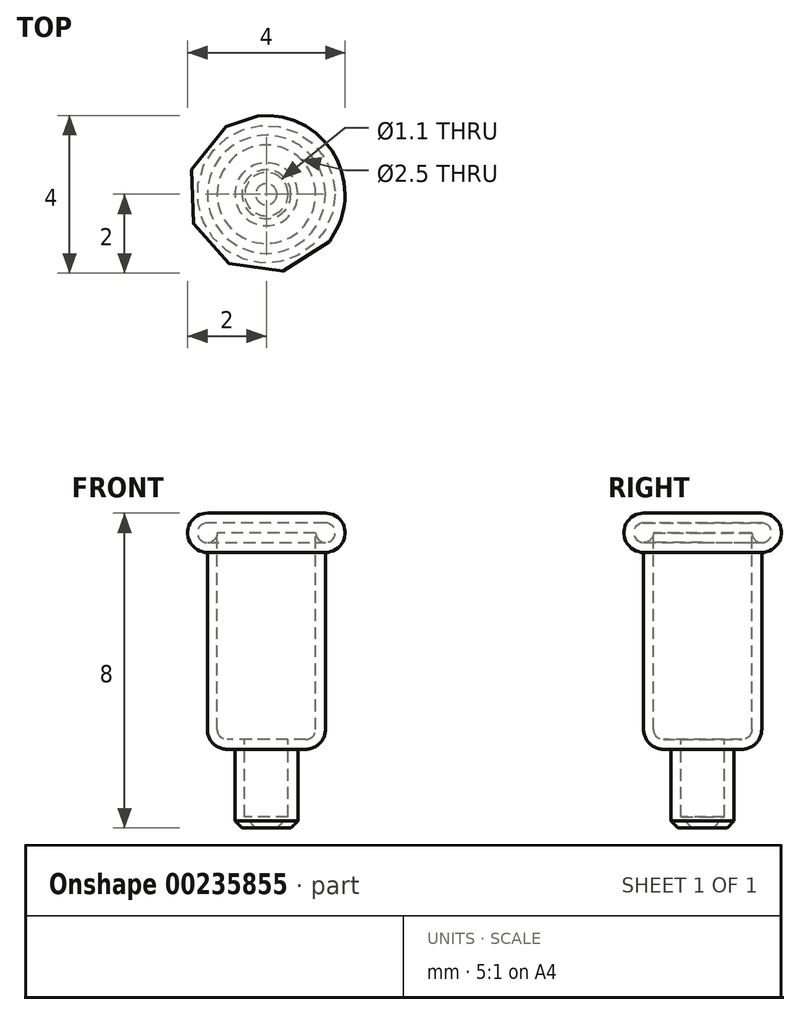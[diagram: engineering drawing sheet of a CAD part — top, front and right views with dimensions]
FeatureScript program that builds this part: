
annotation { "Feature Type Name" : "Feature", "Feature Type Description" : "" }
export const myFeature = defineFeature(function(context is Context, id is Id, definition is map)
    precondition{}
    {
        {
            var Q0;
            Q0=qCreatedBy(makeId("Front.planeOp"),FACE);
            var sketch = newSketch(context, id + "F0", { "sketchPlane" : qUnion([Q0])});
            skLineSegment(sketch, "E0", {"start": v(0, 0) * mm, "end": v(0, -8) * mm});
            skLineSegment(sketch, "E1", {"start": v(0, 0) * mm, "end": v(-1.5, 0) * mm});
            skLineSegment(sketch, "E2", {"start": v(-2, -0.5) * mm, "end": v(-2, -0.5) * mm});
            skLineSegment(sketch, "E3.0", {"start": v(-1.5, -1) * mm, "end": v(-1.5, -5.5) * mm});
            skLineSegment(sketch, "E4.0", {"start": v(-0.8, -6) * mm, "end": v(-0.8, -7.82) * mm});
            skLineSegment(sketch, "E5.0", {"start": v(-0.8, -6) * mm, "end": v(-1, -6) * mm});
            skLineSegment(sketch, "E6.trimOffspring", {"start": v(-1.5, -1) * mm, "end": v(-1.5, -1) * mm});
            skLineSegment(sketch, "E7.0", {"start": v(-1.25, -0.5) * mm, "end": v(-1.25, -5.5) * mm});
            skLineSegment(sketch, "E8.0", {"start": v(0, -0.25) * mm, "end": v(-1.5, -0.25) * mm});
            skLineSegment(sketch, "E9", {"start": v(-0.55, -5.75) * mm, "end": v(-1, -5.75) * mm});
            skLineSegment(sketch, "E10", {"start": v(-1.25, -0.5) * mm, "end": v(0, -0.5) * mm, "construction": true});
            skArc(sketch, "E11.filletArc", {"start": v(-1.5, 0) * mm, "mid": v(-1.85, -0.15) * mm, "end": v(-2, -0.5) * mm});
            skPoint(sketch, "E12.visualSharp", {"position": v(-2, -1) * mm});
            skArc(sketch, "E12.filletArc", {"start": v(-2, -0.5) * mm, "mid": v(-1.85, -0.85) * mm, "end": v(-1.5, -1) * mm});
            skArc(sketch, "E13", {"start": v(-1.5, -0.25) * mm, "mid": v(-1.68, -0.68) * mm, "end": v(-1.25, -0.5) * mm});
            skArc(sketch, "E14.filletArc", {"start": v(-1.5, -5.5) * mm, "mid": v(-1.35, -5.85) * mm, "end": v(-1, -6) * mm});
            skArc(sketch, "E15", {"start": v(-1.25, -5.5) * mm, "mid": v(-1.18, -5.68) * mm, "end": v(-1, -5.75) * mm});
            skLineSegment(sketch, "E16", {"start": v(-0.55, -5.75) * mm, "end": v(0, -5.75) * mm, "construction": true});
            skLineSegment(sketch, "E17.0", {"start": v(-0.55, -5.75) * mm, "end": v(-0.55, -7.72) * mm});
            skLineSegment(sketch, "E18", {"start": v(-0.27, -8) * mm, "end": v(-0.62, -8) * mm, "construction": true});
            skLineSegment(sketch, "E19", {"start": v(-0.62, -8) * mm, "end": v(-0.8, -7.82) * mm});
            skLineSegment(sketch, "E20", {"start": v(-0.27, -8) * mm, "end": v(-0.55, -7.72) * mm});
            skLineSegment(sketch, "E21", {"start": v(-0.27, -8) * mm, "end": v(-0.6, -8) * mm});
            skLineSegment(sketch, "E22", {"start": v(-0.6, -8) * mm, "end": v(-0.6, -6) * mm, "construction": true});
            skLineSegment(sketch, "E23", {"start": v(-0.8, -6) * mm, "end": v(0, -6) * mm, "construction": true});
            skLineSegment(sketch, "E24", {"start": v(-0.62, -8) * mm, "end": v(-0.27, -8) * mm});
            skSolve(sketch);
        }
        {
            var Q0;
            Q0 = qSketchRegion(id + "F0", true);
            var Q1;
            Q1=sQuery(id+"F0.wireOp",EDGE,"E0");
            revolve(context, id + "F1", {"entities" : qUnion([Q0]), "axis" : qUnion([Q1]), "revolveType" : RevolveType.FULL});
        }
    });
